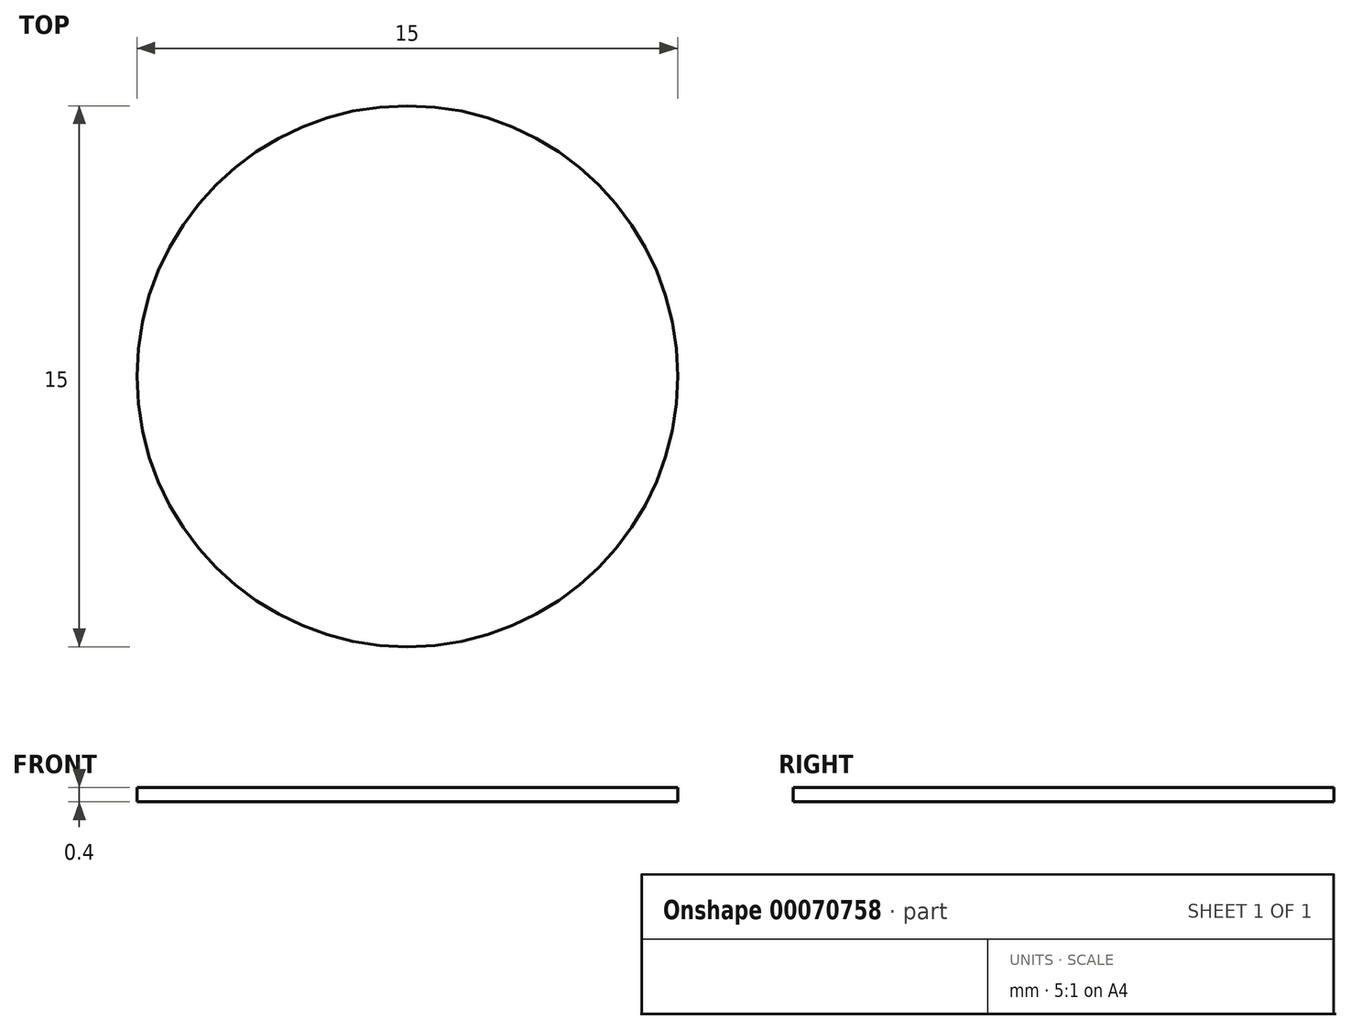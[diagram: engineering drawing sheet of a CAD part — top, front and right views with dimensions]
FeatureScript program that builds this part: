
annotation { "Feature Type Name" : "Feature", "Feature Type Description" : "" }
export const myFeature = defineFeature(function(context is Context, id is Id, definition is map)
    precondition{}
    {
        {
            var Q0;
            Q0=qCreatedBy(makeId("Top.planeOp"),FACE);
            var sketch = newSketch(context, id + "F0", { "sketchPlane" : qUnion([Q0])});
            skCircle(sketch, "E0", {"center": v(0.13, -0.65) * mm, "radius": 7.5 * mm});
            skSolve(sketch);
        }
        {
            var Q0;
            Q0=makeQuery(id+"F0.imprint","IMPRINT",FACE,{"disambiguationData":[TD([[makeQuery(id+"F0.imprint","IMPRINT",EDGE,{"derivedFrom":sQuery(id+"F0.wireOp",EDGE,"E0")}),1.0]])]});
            extrude(context, id + "F1", {"entities" : qUnion([Q0]), "depth" : 0.4 * mm});
        }
    });
